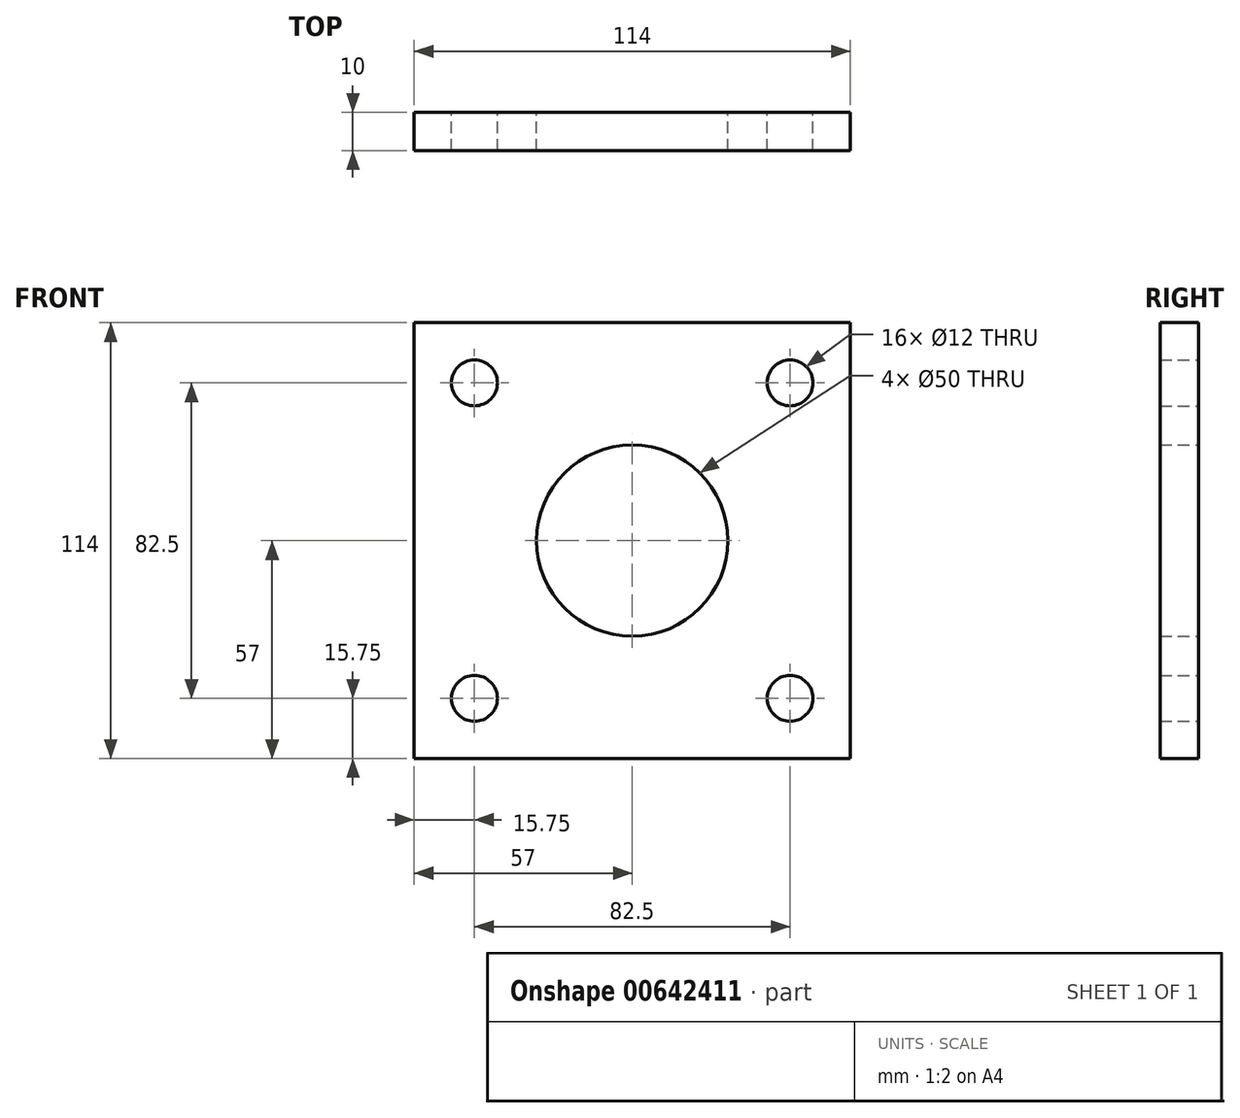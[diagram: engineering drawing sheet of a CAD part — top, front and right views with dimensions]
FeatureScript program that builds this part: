
annotation { "Feature Type Name" : "Feature", "Feature Type Description" : "" }
export const myFeature = defineFeature(function(context is Context, id is Id, definition is map)
    precondition{}
    {
        {
            var Q0;
            Q0=qCreatedBy(makeId("Front.planeOp"),FACE);
            var sketch = newSketch(context, id + "F0", { "sketchPlane" : qUnion([Q0])});
            skLineSegment(sketch, "E0.bottom", {"start": v(57, -57) * mm, "end": v(-57, -57) * mm});
            skLineSegment(sketch, "E0.top", {"start": v(57, 57) * mm, "end": v(-57, 57) * mm});
            skLineSegment(sketch, "E0.left", {"start": v(57, -57) * mm, "end": v(57, 57) * mm});
            skLineSegment(sketch, "E0.right", {"start": v(-57, -57) * mm, "end": v(-57, 57) * mm});
            skPoint(sketch, "E0.middle", {"position": v(0, 0) * mm});
            skCircle(sketch, "E1", {"center": v(-41.25, 41.25) * mm, "radius": 6 * mm});
            skCircle(sketch, "E2.MirrorC", {"center": v(41.25, 41.25) * mm, "radius": 6 * mm});
            skCircle(sketch, "E3.MirrorC", {"center": v(-41.25, -41.25) * mm, "radius": 6 * mm});
            skCircle(sketch, "E4.MirrorC", {"center": v(41.25, -41.25) * mm, "radius": 6 * mm});
            skCircle(sketch, "E5", {"center": v(0, 0) * mm, "radius": 25 * mm});
            skSolve(sketch);
        }
        {
            var Q0;
            Q0=makeQuery(id+"F0.imprint","IMPRINT",FACE,{"disambiguationData":[TD([[makeQuery(id+"F0.imprint","IMPRINT",EDGE,{"derivedFrom":sQuery(id+"F0.wireOp",EDGE,"E0.bottom")}),-1.0]])]});
            extrude(context, id + "F1", {"entities" : qUnion([Q0]), "depth" : 10 * mm, "offsetDistance" : 25 * mm});
        }
    });
